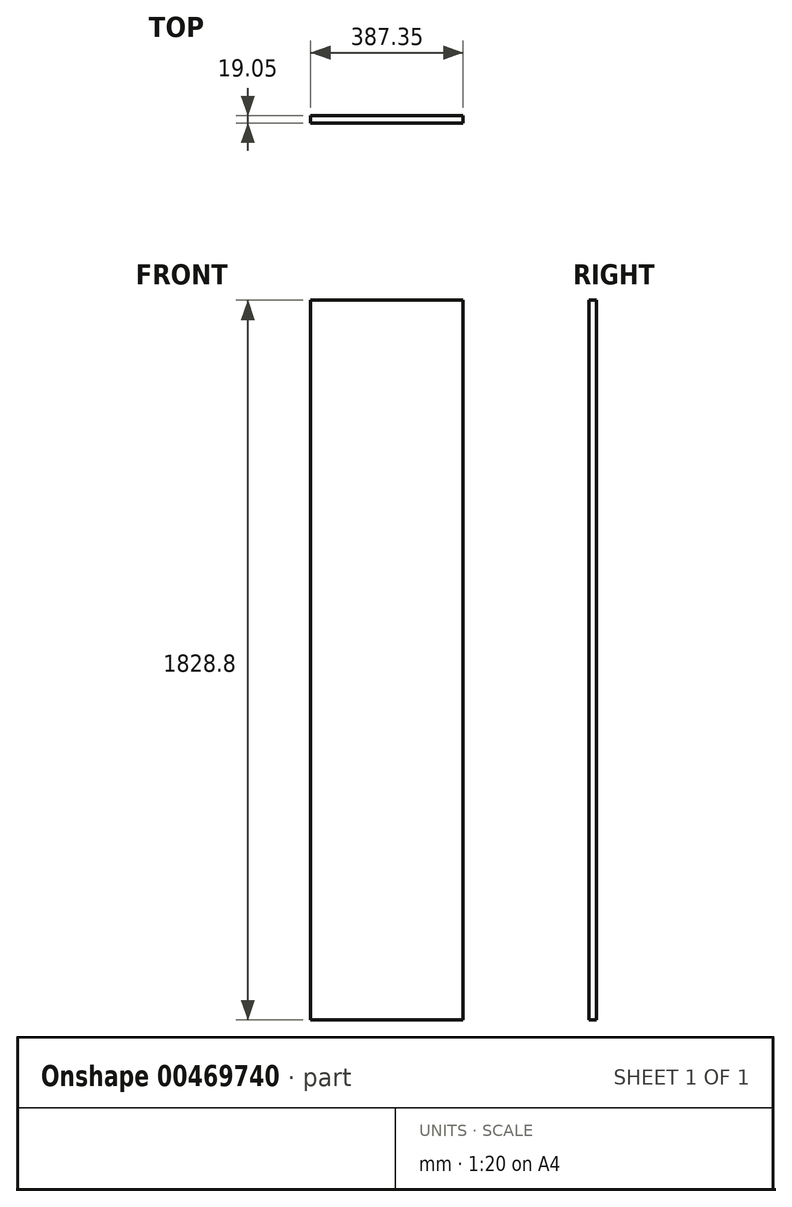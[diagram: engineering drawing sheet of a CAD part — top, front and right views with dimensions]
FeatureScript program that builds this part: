
annotation { "Feature Type Name" : "Feature", "Feature Type Description" : "" }
export const myFeature = defineFeature(function(context is Context, id is Id, definition is map)
    precondition{}
    {
        {
            var Q0;
            Q0=qCreatedBy(makeId("Front.planeOp"),FACE);
            var sketch = newSketch(context, id + "F0", { "sketchPlane" : qUnion([Q0])});
            skLineSegment(sketch, "E0.bottom", {"start": v(0, 0) * mm, "end": v(387.35, 0) * mm});
            skLineSegment(sketch, "E0.top", {"start": v(0, 1828.8) * mm, "end": v(387.35, 1828.8) * mm});
            skLineSegment(sketch, "E0.left", {"start": v(0, 0) * mm, "end": v(0, 1828.8) * mm});
            skLineSegment(sketch, "E0.right", {"start": v(387.35, 0) * mm, "end": v(387.35, 1828.8) * mm});
            skSolve(sketch);
        }
        {
            var Q0;
            Q0=makeQuery(id+"F0.imprint","IMPRINT",FACE,{"disambiguationData":[TD([[makeQuery(id+"F0.imprint","IMPRINT",EDGE,{"derivedFrom":sQuery(id+"F0.wireOp",EDGE,"E0.bottom")}),1.0]])]});
            extrude(context, id + "F1", {"entities" : qUnion([Q0]), "depth" : 19.05 * mm, "offsetDistance" : 25.4 * mm});
        }
    });
